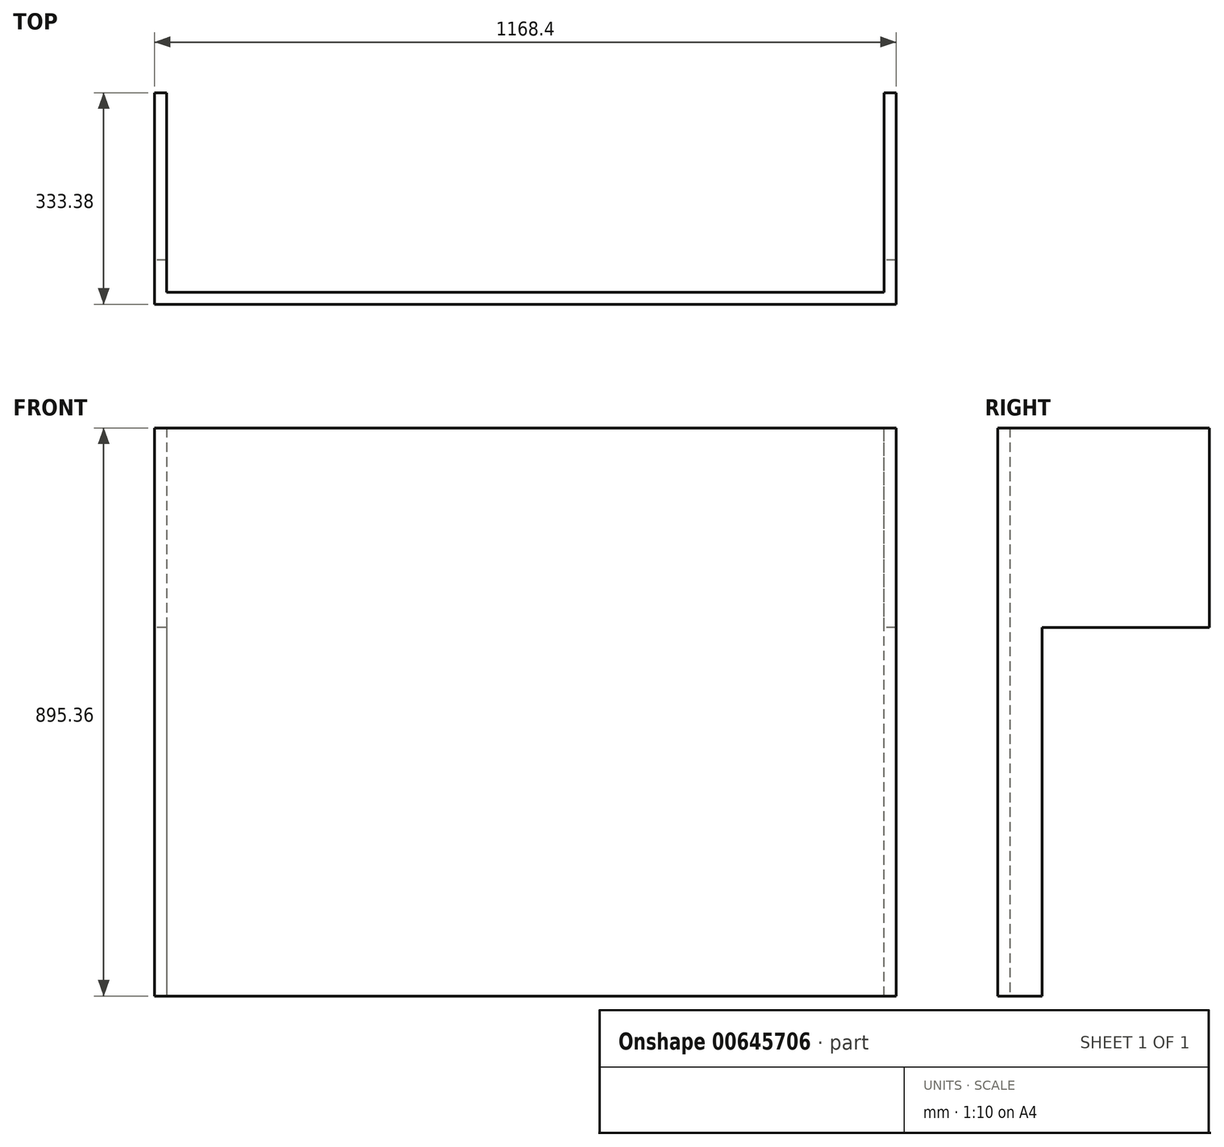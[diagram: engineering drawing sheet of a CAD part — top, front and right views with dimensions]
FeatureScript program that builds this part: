
annotation { "Feature Type Name" : "Feature", "Feature Type Description" : "" }
export const myFeature = defineFeature(function(context is Context, id is Id, definition is map)
    precondition{}
    {
        {
            var Q0;
            Q0=qCreatedBy(makeId("Front.planeOp"),FACE);
            var sketch = newSketch(context, id + "F0", { "sketchPlane" : qUnion([Q0])});
            skLineSegment(sketch, "E0.bottom", {"start": v(-584.2, 371.48) * mm, "end": v(584.2, 371.48) * mm});
            skLineSegment(sketch, "E0.top", {"start": v(-584.2, -371.48) * mm, "end": v(584.2, -371.48) * mm});
            skLineSegment(sketch, "E0.left", {"start": v(-584.2, 371.48) * mm, "end": v(-584.2, -371.48) * mm});
            skLineSegment(sketch, "E0.right", {"start": v(584.2, 371.48) * mm, "end": v(584.2, -371.48) * mm});
            skPoint(sketch, "E0.middle", {"position": v(0, 0) * mm});
            skSolve(sketch);
        }
        {
            var Q0;
            Q0=makeQuery(id+"F0.imprint","IMPRINT",FACE,{"disambiguationData":[TD([[makeQuery(id+"F0.imprint","IMPRINT",EDGE,{"derivedFrom":sQuery(id+"F0.wireOp",EDGE,"E0.bottom")}),-1.0]])]});
            extrude(context, id + "F1", {"entities" : qUnion([Q0]), "depth" : 19.05 * mm, "offsetDistance" : 25.4 * mm});
        }
        {
            var Q0;
            Q0=makeQuery(id+"F1.opExtrude","CAP_FACE",FACE,{"disambiguationData":[OSD([sQuery(id+"F0.wireOp",EDGE,"E0.bottom"),sQuery(id+"F0.wireOp",EDGE,"E0.top"),sQuery(id+"F0.wireOp",EDGE,"E0.left"),sQuery(id+"F0.wireOp",EDGE,"E0.right")])],"isStart":true});
            var sketch = newSketch(context, id + "F2", { "sketchPlane" : qUnion([Q0])});
            skLineSegment(sketch, "E1.bottom", {"start": v(-584.2, -371.48) * mm, "end": v(-565.15, -371.48) * mm});
            skLineSegment(sketch, "E1.top", {"start": v(-584.2, 371.48) * mm, "end": v(-565.15, 371.48) * mm});
            skLineSegment(sketch, "E1.left", {"start": v(-584.2, -371.48) * mm, "end": v(-584.2, 371.48) * mm});
            skLineSegment(sketch, "E1.right", {"start": v(-565.15, -371.48) * mm, "end": v(-565.15, 371.48) * mm});
            skLineSegment(sketch, "E2.bottom", {"start": v(584.2, 371.48) * mm, "end": v(565.15, 371.48) * mm});
            skLineSegment(sketch, "E2.top", {"start": v(584.2, -371.48) * mm, "end": v(565.15, -371.48) * mm});
            skLineSegment(sketch, "E2.left", {"start": v(584.2, 371.48) * mm, "end": v(584.2, -371.48) * mm});
            skLineSegment(sketch, "E2.right", {"start": v(565.15, 371.48) * mm, "end": v(565.15, -371.48) * mm});
            skSolve(sketch);
        }
        {
            var Q0;
            Q0=makeQuery(id+"F2.imprint","IMPRINT",FACE,{"disambiguationData":[TD([[makeQuery(id+"F2.imprint","IMPRINT",EDGE,{"derivedFrom":sQuery(id+"F2.wireOp",EDGE,"E1.bottom")}),-1.0]])]});
            var Q1;
            Q1=makeQuery(id+"F2.imprint","IMPRINT",FACE,{"disambiguationData":[TD([[makeQuery(id+"F2.imprint","IMPRINT",EDGE,{"derivedFrom":sQuery(id+"F2.wireOp",EDGE,"E2.bottom")}),1.0]])]});
            extrude(context, id + "F3", {"entities" : qUnion([Q0, Q1]), "operationType" : NewBodyOperationType.ADD, "depth" : 50.8 * mm, "offsetDistance" : 25.4 * mm});
        }
        {
            var Q0;
            Q0=makeQuery(id+"F3.opExtrude","CAP_FACE",FACE,{"disambiguationData":[OSD([sQuery(id+"F2.wireOp",EDGE,"E1.bottom"),sQuery(id+"F2.wireOp",EDGE,"E1.top"),sQuery(id+"F2.wireOp",EDGE,"E1.left"),sQuery(id+"F2.wireOp",EDGE,"E1.right")])],"isStart":false});
            var sketch = newSketch(context, id + "F4", { "sketchPlane" : qUnion([Q0])});
            skLineSegment(sketch, "E3.bottom", {"start": v(-584.2, 371.48) * mm, "end": v(-565.15, 371.48) * mm});
            skLineSegment(sketch, "E3.top", {"start": v(-584.2, 57.15) * mm, "end": v(-565.15, 57.15) * mm});
            skLineSegment(sketch, "E3.left", {"start": v(-584.2, 371.48) * mm, "end": v(-584.2, 57.15) * mm});
            skLineSegment(sketch, "E3.right", {"start": v(-565.15, 371.48) * mm, "end": v(-565.15, 57.15) * mm});
            skSolve(sketch);
        }
        {
            var Q0;
            Q0=makeQuery(id+"F4.imprint","IMPRINT",FACE,{"disambiguationData":[TD([[makeQuery(id+"F4.imprint","IMPRINT",EDGE,{"derivedFrom":sQuery(id+"F4.wireOp",EDGE,"E3.bottom")}),1.0]])]});
            extrude(context, id + "F5", {"entities" : qUnion([Q0]), "operationType" : NewBodyOperationType.ADD, "depth" : 263.52 * mm, "offsetDistance" : 25.4 * mm});
        }
        {
            var Q0;
            Q0=makeQuery(id+"F3.opExtrude","CAP_FACE",FACE,{"disambiguationData":[OSD([sQuery(id+"F2.wireOp",EDGE,"E2.bottom"),sQuery(id+"F2.wireOp",EDGE,"E2.top"),sQuery(id+"F2.wireOp",EDGE,"E2.left"),sQuery(id+"F2.wireOp",EDGE,"E2.right")])],"isStart":false});
            var sketch = newSketch(context, id + "F6", { "sketchPlane" : qUnion([Q0])});
            skLineSegment(sketch, "E4.bottom", {"start": v(565.15, 371.48) * mm, "end": v(584.2, 371.48) * mm});
            skLineSegment(sketch, "E4.top", {"start": v(565.15, 57.15) * mm, "end": v(584.2, 57.15) * mm});
            skLineSegment(sketch, "E4.left", {"start": v(565.15, 371.48) * mm, "end": v(565.15, 57.15) * mm});
            skLineSegment(sketch, "E4.right", {"start": v(584.2, 371.48) * mm, "end": v(584.2, 57.15) * mm});
            skSolve(sketch);
        }
        {
            var Q0;
            Q0=makeQuery(id+"F6.imprint","IMPRINT",FACE,{"disambiguationData":[TD([[makeQuery(id+"F6.imprint","IMPRINT",EDGE,{"derivedFrom":sQuery(id+"F6.wireOp",EDGE,"E4.bottom")}),1.0]])]});
            extrude(context, id + "F7", {"entities" : qUnion([Q0]), "operationType" : NewBodyOperationType.ADD, "depth" : 263.52 * mm, "offsetDistance" : 25.4 * mm});
        }
        {
            var Q0;
            Q0=makeQuery(id+"F3.boolean.opBoolean","MERGE",FACE,{"derivedFrom":[makeQuery(id+"F1.opExtrude","SWEPT_FACE",FACE,{"disambiguationData":[OSD([sQuery(id+"F0.wireOp",EDGE,"E0.top")])]}),makeQuery(id+"F3.opExtrude","SWEPT_FACE",FACE,{"disambiguationData":[OSD([sQuery(id+"F2.wireOp",EDGE,"E1.bottom")])]}),makeQuery(id+"F3.opExtrude","SWEPT_FACE",FACE,{"disambiguationData":[OSD([sQuery(id+"F2.wireOp",EDGE,"E2.top")])]})]});
            extrude(context, id + "F8", {"entities" : qUnion([Q0]), "operationType" : NewBodyOperationType.ADD, "depth" : 152.4 * mm, "offsetDistance" : 25.4 * mm});
        }
    });
